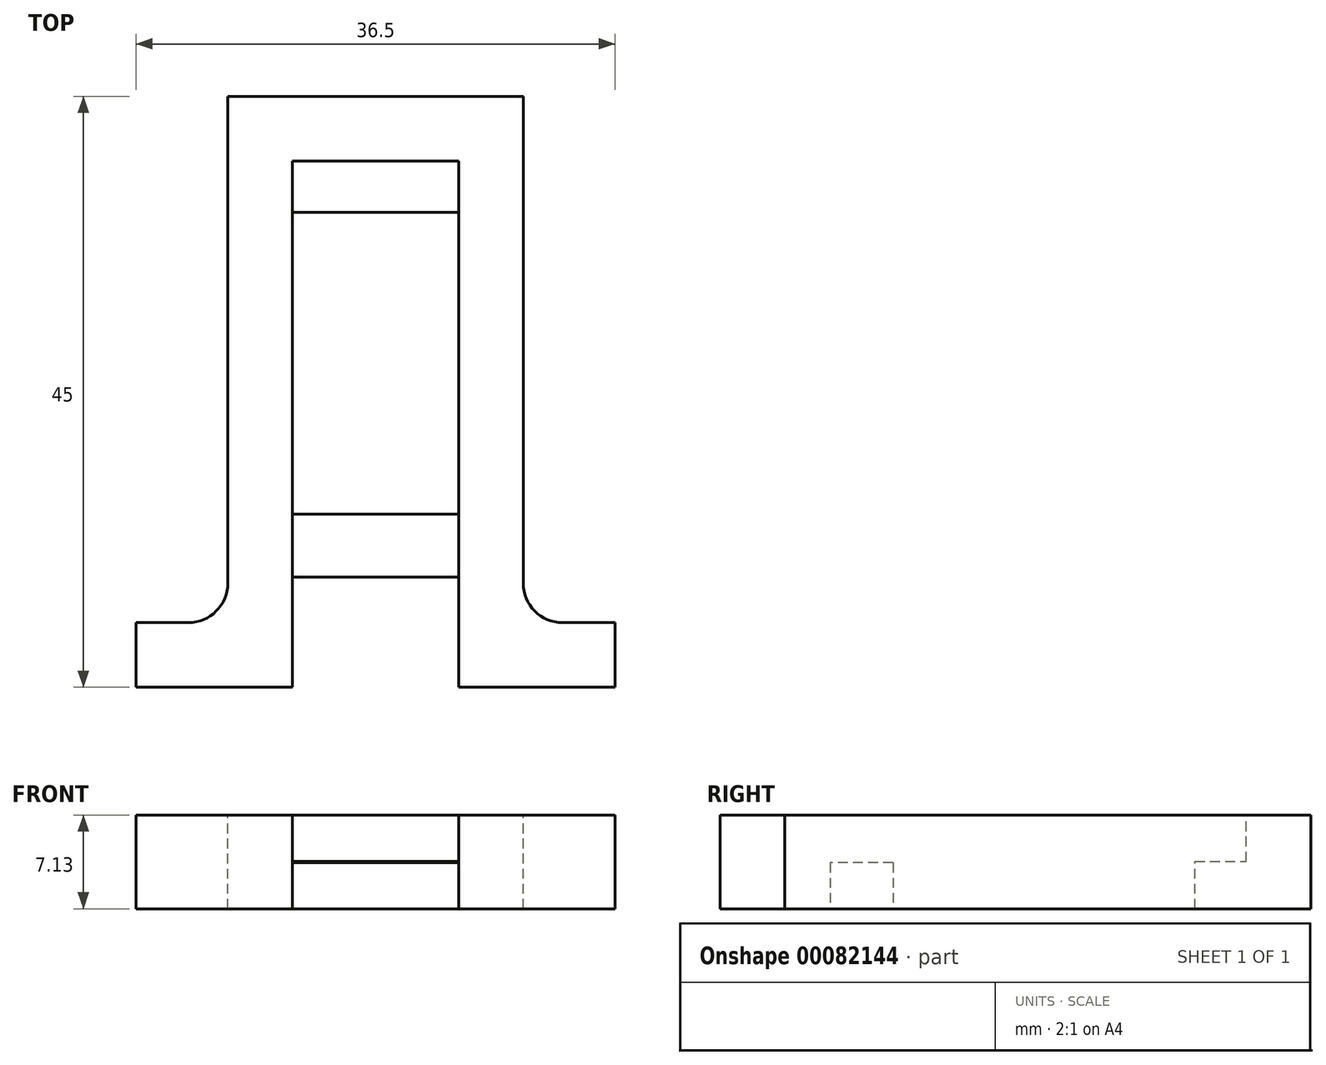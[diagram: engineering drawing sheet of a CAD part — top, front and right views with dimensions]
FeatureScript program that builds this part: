
annotation { "Feature Type Name" : "Feature", "Feature Type Description" : "" }
export const myFeature = defineFeature(function(context is Context, id is Id, definition is map)
    precondition{}
    {
        {
            var Q0;
            Q0=qCreatedBy(makeId("Top.planeOp"),FACE);
            var sketch = newSketch(context, id + "F0", { "sketchPlane" : qUnion([Q0])});
            skLineSegment(sketch, "E0.bottom", {"start": v(-15.59, 27.76) * mm, "end": v(20.91, 27.76) * mm});
            skLineSegment(sketch, "E0.top", {"start": v(-15.59, -17.24) * mm, "end": v(20.91, -17.24) * mm});
            skLineSegment(sketch, "E0.left", {"start": v(-15.59, 27.76) * mm, "end": v(-15.59, -17.24) * mm});
            skLineSegment(sketch, "E0.right", {"start": v(20.91, 27.76) * mm, "end": v(20.91, -17.24) * mm});
            skSolve(sketch);
        }
        {
            var Q0;
            Q0=qSketchRegion(id+"F0",true);
            extrude(context, id + "F1", {"entities" : qUnion([Q0]), "depth" : 7.13 * mm});
        }
        {
            var Q0;
            Q0=makeQuery(id+"F1.opExtrude","CAP_FACE",FACE,{"disambiguationData":[OSD([sQuery(id+"F0.wireOp",EDGE,"E0.bottom"),sQuery(id+"F0.wireOp",EDGE,"E0.top"),sQuery(id+"F0.wireOp",EDGE,"E0.left"),sQuery(id+"F0.wireOp",EDGE,"E0.right")])],"isStart":false});
            var sketch = newSketch(context, id + "F2", { "sketchPlane" : qUnion([Q0])});
            skLineSegment(sketch, "E1.bottom", {"start": v(-15.59, 27.76) * mm, "end": v(-8.59, 27.76) * mm});
            skLineSegment(sketch, "E1.top", {"start": v(-15.59, -12.32) * mm, "end": v(-8.59, -12.32) * mm});
            skLineSegment(sketch, "E1.left", {"start": v(-15.59, 27.76) * mm, "end": v(-15.59, -12.32) * mm});
            skLineSegment(sketch, "E1.right", {"start": v(-8.59, 27.76) * mm, "end": v(-8.59, -12.32) * mm});
            skLineSegment(sketch, "E2.bottom", {"start": v(20.91, 27.76) * mm, "end": v(13.91, 27.76) * mm});
            skLineSegment(sketch, "E2.top", {"start": v(20.91, -12.32) * mm, "end": v(13.91, -12.32) * mm});
            skLineSegment(sketch, "E2.left", {"start": v(20.91, 27.76) * mm, "end": v(20.91, -12.32) * mm});
            skLineSegment(sketch, "E2.right", {"start": v(13.91, 27.76) * mm, "end": v(13.91, -12.32) * mm});
            skSolve(sketch);
        }
        {
            var Q0;
            Q0=qSketchRegion(id+"F2",true);
            extrude(context, id + "F3", {"entities" : qUnion([Q0]), "operationType" : NewBodyOperationType.REMOVE, "oppositeDirection" : true, "depth" : 7.13 * mm});
        }
        {
            var Q0;
            Q0=makeQuery(id+"F1.opExtrude","CAP_FACE",FACE,{"disambiguationData":[OSD([sQuery(id+"F0.wireOp",EDGE,"E0.bottom"),sQuery(id+"F0.wireOp",EDGE,"E0.top"),sQuery(id+"F0.wireOp",EDGE,"E0.left"),sQuery(id+"F0.wireOp",EDGE,"E0.right")])],"isStart":false});
            var sketch = newSketch(context, id + "F4", { "sketchPlane" : qUnion([Q0])});
            skLineSegment(sketch, "E3.bottom", {"start": v(-3.67, 18.93) * mm, "end": v(9, 18.93) * mm});
            skLineSegment(sketch, "E3.top", {"start": v(-3.67, -17.24) * mm, "end": v(9, -17.24) * mm});
            skLineSegment(sketch, "E3.left", {"start": v(-3.67, 18.93) * mm, "end": v(-3.67, -17.24) * mm});
            skLineSegment(sketch, "E3.right", {"start": v(9, 18.93) * mm, "end": v(9, -17.24) * mm});
            skSolve(sketch);
        }
        {
            var Q0;
            Q0=qSketchRegion(id+"F4",true);
            extrude(context, id + "F5", {"entities" : qUnion([Q0]), "operationType" : NewBodyOperationType.REMOVE, "oppositeDirection" : true, "depth" : 7.13 * mm});
        }
        {
            var Q0;
            Q0=makeQuery(id+"F1.opExtrude","CAP_FACE",FACE,{"disambiguationData":[OSD([sQuery(id+"F0.wireOp",EDGE,"E0.bottom"),sQuery(id+"F0.wireOp",EDGE,"E0.top"),sQuery(id+"F0.wireOp",EDGE,"E0.left"),sQuery(id+"F0.wireOp",EDGE,"E0.right")])],"isStart":false});
            var sketch = newSketch(context, id + "F6", { "sketchPlane" : qUnion([Q0])});
            skLineSegment(sketch, "E4.bottom", {"start": v(-3.67, 18.93) * mm, "end": v(9, 18.93) * mm});
            skLineSegment(sketch, "E4.top", {"start": v(-3.67, 22.84) * mm, "end": v(9, 22.84) * mm});
            skLineSegment(sketch, "E4.left", {"start": v(-3.67, 18.93) * mm, "end": v(-3.67, 22.84) * mm});
            skLineSegment(sketch, "E4.right", {"start": v(9, 18.93) * mm, "end": v(9, 22.84) * mm});
            skSolve(sketch);
        }
        {
            var Q0;
            Q0=qSketchRegion(id+"F6",true);
            extrude(context, id + "F7", {"entities" : qUnion([Q0]), "operationType" : NewBodyOperationType.REMOVE, "oppositeDirection" : true, "depth" : 3.53 * mm});
        }
        {
            var Q0;
            Q0=makeQuery(id+"F1.opExtrude","CAP_FACE",FACE,{"disambiguationData":[OSD([sQuery(id+"F0.wireOp",EDGE,"E0.bottom"),sQuery(id+"F0.wireOp",EDGE,"E0.top"),sQuery(id+"F0.wireOp",EDGE,"E0.left"),sQuery(id+"F0.wireOp",EDGE,"E0.right")])],"isStart":true});
            var sketch = newSketch(context, id + "F8", { "sketchPlane" : qUnion([Q0])});
            skLineSegment(sketch, "E5.bottom", {"start": v(-3.67, 8.87) * mm, "end": v(9, 8.87) * mm});
            skLineSegment(sketch, "E5.top", {"start": v(-3.67, 4.07) * mm, "end": v(9, 4.07) * mm});
            skLineSegment(sketch, "E5.left", {"start": v(-3.67, 8.87) * mm, "end": v(-3.67, 4.07) * mm});
            skLineSegment(sketch, "E5.right", {"start": v(9, 8.87) * mm, "end": v(9, 4.07) * mm});
            skSolve(sketch);
        }
        {
            var Q0;
            Q0=qSketchRegion(id+"F8",true);
            extrude(context, id + "F9", {"entities" : qUnion([Q0]), "operationType" : NewBodyOperationType.ADD, "oppositeDirection" : true, "depth" : 3.5 * mm});
        }
        {
            var Q0;
            Q0=makeQuery(id+"F3.boolean.opBoolean","COPY",EDGE,{"derivedFrom":makeQuery(id+"F3.opExtrude","SWEPT_EDGE",EDGE,{"disambiguationData":[OSD([sQuery(id+"F2.wireOp",EDGE,"E2.top"),sQuery(id+"F2.wireOp",EDGE,"E2.right")])]})});
            var Q1;
            Q1=makeQuery(id+"F3.boolean.opBoolean","COPY",EDGE,{"derivedFrom":makeQuery(id+"F3.opExtrude","SWEPT_EDGE",EDGE,{"disambiguationData":[OSD([sQuery(id+"F2.wireOp",EDGE,"E1.top"),sQuery(id+"F2.wireOp",EDGE,"E1.right")])]})});
            fillet(context, id + "F10", {"entities" : qUnion([Q0, Q1]), "radius" : 3 * mm, "tangentPropagation" : true, "allowEdgeOverflow" : false});
        }
    });
